# Revit family: Bernhardt_Design-Tables-Conference-Playbook_4star
name_source: partatom
category: Furniture
revit_build: Autodesk Revit 2016 (Build: 20150714_1515(x64)
units: mm (PartAtom-declared; Revit-internal decimal feet)

## family parameters
Always vertical = Yes
Cut with Voids When Loaded = No
OmniClass Number = 23.40.20.00
OmniClass Title = General Furniture and Specialties
Room Calculation Point = No
Shared = No
Work Plane-Based = No

## types (20) — shared parameters
Casters = <By Category>
Manufacturer = Bernhardt Design
Model = Playbook
URL = http://www.bernhardtdesign.com

## per-type parameters (varying)
| type | Base type | Catalog | SKU | Table type | height_tabletop |
| Playbook - 4-star 36" arched square 42" bar height | det 01.1 : bar height | PKS-BAA-4B | PKS-BAA-4B | det_tabletop : arched square 36" | 41.043 " |
| Playbook - 4-star 36" radius square 42" bar height | det 01.1 : bar height | PKS-CAA-4B | PKS-CAA-4B | det_tabletop : radius square 36" | 41.043 " |
| Playbook - 4-star 36" round 42" bar height | det 01.1 : bar height | PKS-AAA-4B | PKS-AAA-4B | det_tabletop : round 36" | 41.043 " |
| Playbook - 4-star 36" square 42" bar height | det 01.1 : bar height | PKS-DAA-4B | PKS-DAA-4B | det_tabletop : square 36" | 41.043 " |
| Playbook - 4-star 36" round 29.5" conference height | det 01.1 : conference height | PKS-AAA-4C | PKS-AAA-4C | det_tabletop : round 36" | 28.512 " |
| Playbook - 4-star 36" arched square 29.5" conference height | det 01.1 : conference height | PKS-BAA-4C | PKS-BAA-4C | det_tabletop : arched square 36" | 28.512 " |
| Playbook - 4-star 36" radius square 29.5" conference height | det 01.1 : conference height | PKS-CAA-4C | PKS-CAA-4C | det_tabletop : radius square 36" | 28.512 " |
| Playbook - 4-star 36" square 29.5" conference height | det 01.1 : conference height | PKS-DAA-4C | PKS-DAA-4C | det_tabletop : square 36" | 28.512 " |
| Playbook - 4-star mobile 36" round 29.5" conference height | det 01.1 : conference height - mobile base | PKS-AAA-4M | PKS-AAA-4M | det_tabletop : round 36" | 28.512 " |
| Playbook - 4-star mobile 36" arched square 29.5" conference height | det 01.1 : conference height - mobile base | PKS-BAA-4M | PKS-BAA-4M | det_tabletop : arched square 36" | 28.512 " |
| Playbook - 4-star mobile 36" radius square 29.5" conference height | det 01.1 : conference height - mobile base | PKS-CAA-4M | PKS-CAA-4M | det_tabletop : radius square 36" | 28.512 " |
| Playbook - 4-star mobile 36" square 29.5" conference height | det 01.1 : conference height - mobile base | PKS-DAA-4M | PKS-DAA-4M | det_tabletop : square 36" | 28.512 " |
| Playbook - 4-star 36" round 26" lounge height | det 01.1 : lounge height | PKS-AAA-4L | PKS-AAA-4L | det_tabletop : round 36" | 25.02 " |
| Playbook - 4-star 36" arched square 26" lounge height | det 01.1 : lounge height | PKS-BAA-4L | PKS-BAA-4L | det_tabletop : arched square 36" | 25.02 " |
| Playbook - 4-star 36" radius square 26" lounge height | det 01.1 : lounge height | PKS-CAA-4L | PKS-CAA-4L | det_tabletop : radius square 36" | 25.02 " |
| Playbook - 4-star 36" square 26" lounge height | det 01.1 : lounge height | PKS-DAA-4L | PKS-DAA-4L | det_tabletop : square 36" | 25.02 " |
| Playbook - 4-star 36" round 36" counter height | det 01.1 : counter height | PKS-AAA-4T | PKS-AAA-4T | det_tabletop : round 36" | 35.02 " |
| Playbook - 4-star 36" arched square 36" counter height | det 01.1 : counter height | PKS-BAA-4T
PKS-BAA-4T
PKS-BAA-4T
PKS-BAA-4T
PKS-BAA-4T | PKS-BAA-4T
PKS-BAA-4T
PKS-BAA-4T
PKS-BAA-4T
PKS-BAA-4T | det_tabletop : arched square 36" | 35.02 " |
| Playbook - 4-star 36" radius square 36" counter height | det 01.1 : counter height | PKS-CAA-4T | PKS-CAA-4T | det_tabletop : radius square 36" | 35.02 " |
| Playbook - 4-star 36" square 36" counter height | det 01.1 : counter height | PKS-DAA-4T | PKS-DAA-4T | det_tabletop : square 36" | 35.02 " |

## geometry (parser evidence)
native form markers: Sweep x19
no freeform markers — native parametric forms only
